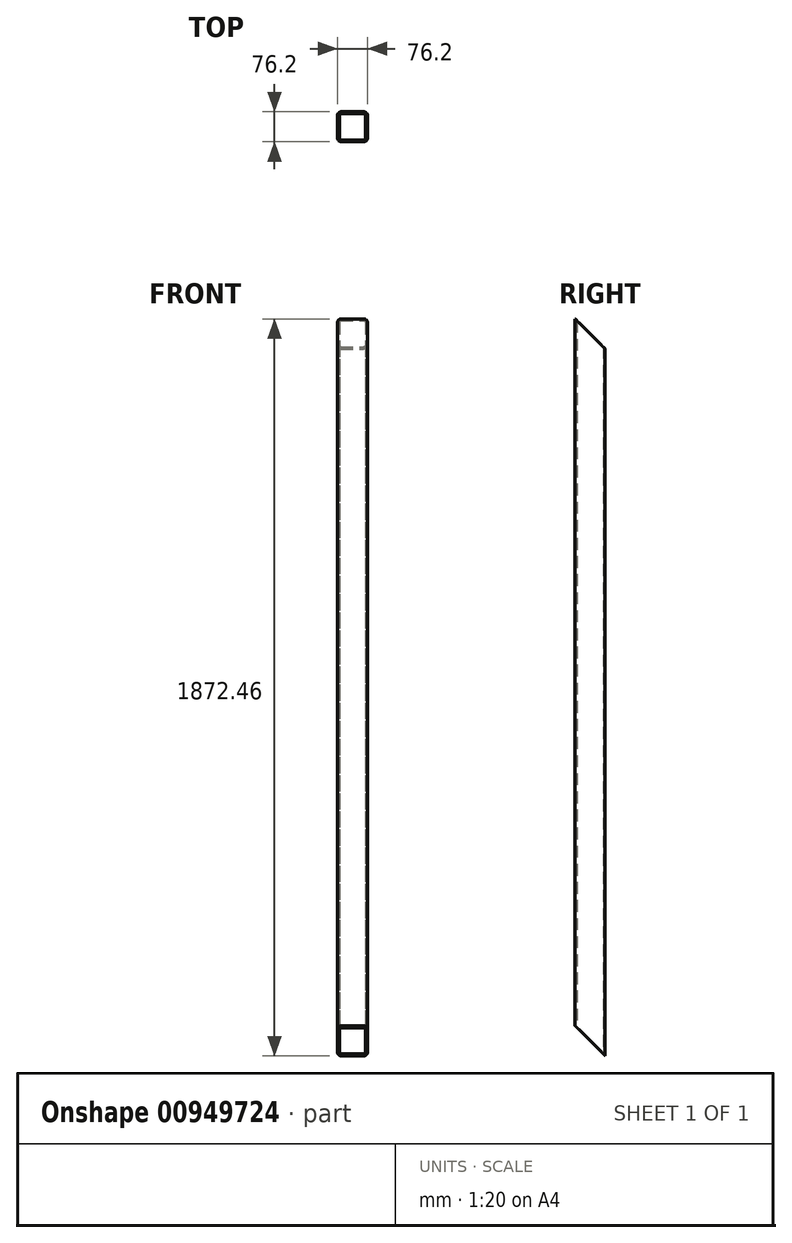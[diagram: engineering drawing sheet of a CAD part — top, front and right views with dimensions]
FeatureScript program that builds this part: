
annotation { "Feature Type Name" : "Feature", "Feature Type Description" : "" }
export const myFeature = defineFeature(function(context is Context, id is Id, definition is map)
    precondition{}
    {
        {
            var Q0;
            Q0=qCreatedBy(makeId("Top.planeOp"),FACE);
            var sketch = newSketch(context, id + "F0", { "sketchPlane" : qUnion([Q0])});
            skLineSegment(sketch, "E0.bottom", {"start": v(-28.58, -38.1) * mm, "end": v(28.58, -38.1) * mm});
            skLineSegment(sketch, "E0.top", {"start": v(-28.58, 38.1) * mm, "end": v(28.58, 38.1) * mm});
            skLineSegment(sketch, "E0.left", {"start": v(-38.1, -28.58) * mm, "end": v(-38.1, 28.58) * mm});
            skLineSegment(sketch, "E0.right", {"start": v(38.1, -28.58) * mm, "end": v(38.1, 28.58) * mm});
            skPoint(sketch, "E0.middle", {"position": v(0, 0) * mm});
            skLineSegment(sketch, "E1.bottom", {"start": v(-28.58, -33.34) * mm, "end": v(28.58, -33.34) * mm});
            skLineSegment(sketch, "E1.top", {"start": v(-28.58, 33.34) * mm, "end": v(28.58, 33.34) * mm});
            skLineSegment(sketch, "E1.left", {"start": v(-33.34, -28.58) * mm, "end": v(-33.34, 28.58) * mm});
            skLineSegment(sketch, "E1.right", {"start": v(33.34, -28.58) * mm, "end": v(33.34, 28.58) * mm});
            skPoint(sketch, "E2.visualSharp", {"position": v(-38.1, 38.1) * mm});
            skArc(sketch, "E2.filletArc", {"start": v(-28.58, 38.1) * mm, "mid": v(-35.31, 35.31) * mm, "end": v(-38.1, 28.58) * mm});
            skPoint(sketch, "E3.visualSharp", {"position": v(-38.1, -38.1) * mm});
            skArc(sketch, "E3.filletArc", {"start": v(-38.1, -28.58) * mm, "mid": v(-35.31, -35.31) * mm, "end": v(-28.58, -38.1) * mm});
            skPoint(sketch, "E4.visualSharp", {"position": v(38.1, -38.1) * mm});
            skArc(sketch, "E4.filletArc", {"start": v(28.58, -38.1) * mm, "mid": v(35.31, -35.31) * mm, "end": v(38.1, -28.58) * mm});
            skPoint(sketch, "E5.visualSharp", {"position": v(38.1, 38.1) * mm});
            skArc(sketch, "E5.filletArc", {"start": v(38.1, 28.58) * mm, "mid": v(35.31, 35.31) * mm, "end": v(28.58, 38.1) * mm});
            skPoint(sketch, "E6.visualSharp", {"position": v(-33.34, 33.34) * mm});
            skArc(sketch, "E6.filletArc", {"start": v(-28.58, 33.34) * mm, "mid": v(-31.94, 31.94) * mm, "end": v(-33.34, 28.58) * mm});
            skPoint(sketch, "E7.visualSharp", {"position": v(-33.34, -33.34) * mm});
            skArc(sketch, "E7.filletArc", {"start": v(-33.34, -28.58) * mm, "mid": v(-31.94, -31.94) * mm, "end": v(-28.58, -33.34) * mm});
            skPoint(sketch, "E8.visualSharp", {"position": v(33.34, -33.34) * mm});
            skArc(sketch, "E8.filletArc", {"start": v(28.58, -33.34) * mm, "mid": v(31.94, -31.94) * mm, "end": v(33.34, -28.58) * mm});
            skPoint(sketch, "E9.visualSharp", {"position": v(33.34, 33.34) * mm});
            skArc(sketch, "E9.filletArc", {"start": v(33.34, 28.58) * mm, "mid": v(31.94, 31.94) * mm, "end": v(28.58, 33.34) * mm});
            skSolve(sketch);
        }
        {
            var Q0;
            Q0 = qSketchRegion(id + "F0", true);
            extrude(context, id + "F1", {"entities" : qUnion([Q0]), "depth" : 1872.46 * mm, "offsetDistance" : 25.4 * mm});
        }
        {
            var Q0;
            Q0=qCreatedBy(makeId("Right.planeOp"),FACE);
            var sketch = newSketch(context, id + "F2", { "sketchPlane" : qUnion([Q0])});
            skLineSegment(sketch, "E10", {"start": v(-38.1, 0) * mm, "end": v(38.1, 0) * mm});
            skLineSegment(sketch, "E11", {"start": v(38.1, 0) * mm, "end": v(-38.1, 76.2) * mm});
            skLineSegment(sketch, "E12", {"start": v(-38.1, 76.2) * mm, "end": v(-38.1, 0) * mm});
            skLineSegment(sketch, "E13", {"start": v(-38.1, 1872.46) * mm, "end": v(38.1, 1872.46) * mm});
            skLineSegment(sketch, "E14", {"start": v(38.1, 1872.46) * mm, "end": v(38.1, 1796.26) * mm});
            skLineSegment(sketch, "E15", {"start": v(38.1, 1796.26) * mm, "end": v(-38.1, 1872.46) * mm});
            skSolve(sketch);
        }
        {
            var Q0;
            Q0 = qSketchRegion(id + "F2", true);
            extrude(context, id + "F3", {"entities" : qUnion([Q0]), "operationType" : NewBodyOperationType.REMOVE, "endBound" : BoundingType.THROUGH_ALL, "oppositeDirection" : true, "depth" : 25.4 * mm, "offsetDistance" : 25.4 * mm, "hasSecondDirection" : true, "secondDirectionBound" : SecondDirectionBoundingType.THROUGH_ALL, "secondDirectionOppositeDirection" : false, "secondDirectionDepth" : 25.4 * mm});
        }
    });
